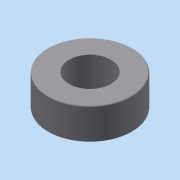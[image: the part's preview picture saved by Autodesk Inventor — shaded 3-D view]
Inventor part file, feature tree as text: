
AUTODESK INVENTOR PART (.ipt)
format: ipt  version: 2015 (Build 190159000, 159)  size: 95,744 bytes
history: native  units: mm
features: extrude x1, fillet x1, sketch x1
ambient origin geometry x8: Origin, YZ Plane, XZ Plane, XY Plane, X Axis, Y Axis, Z Axis, Center Point
bodies: Solid1 (feature_tree)
feature tree (3):
  extrude  "Extrusion1"  Depth=0.1mm
  fillet  "Fillet1"  Radius=3.0mm
  sketch  "Sketch1"  dims[d0=4.0mm d1=8.0mm d2=3.0mm d3=0.0mm d4=0.1mm]
